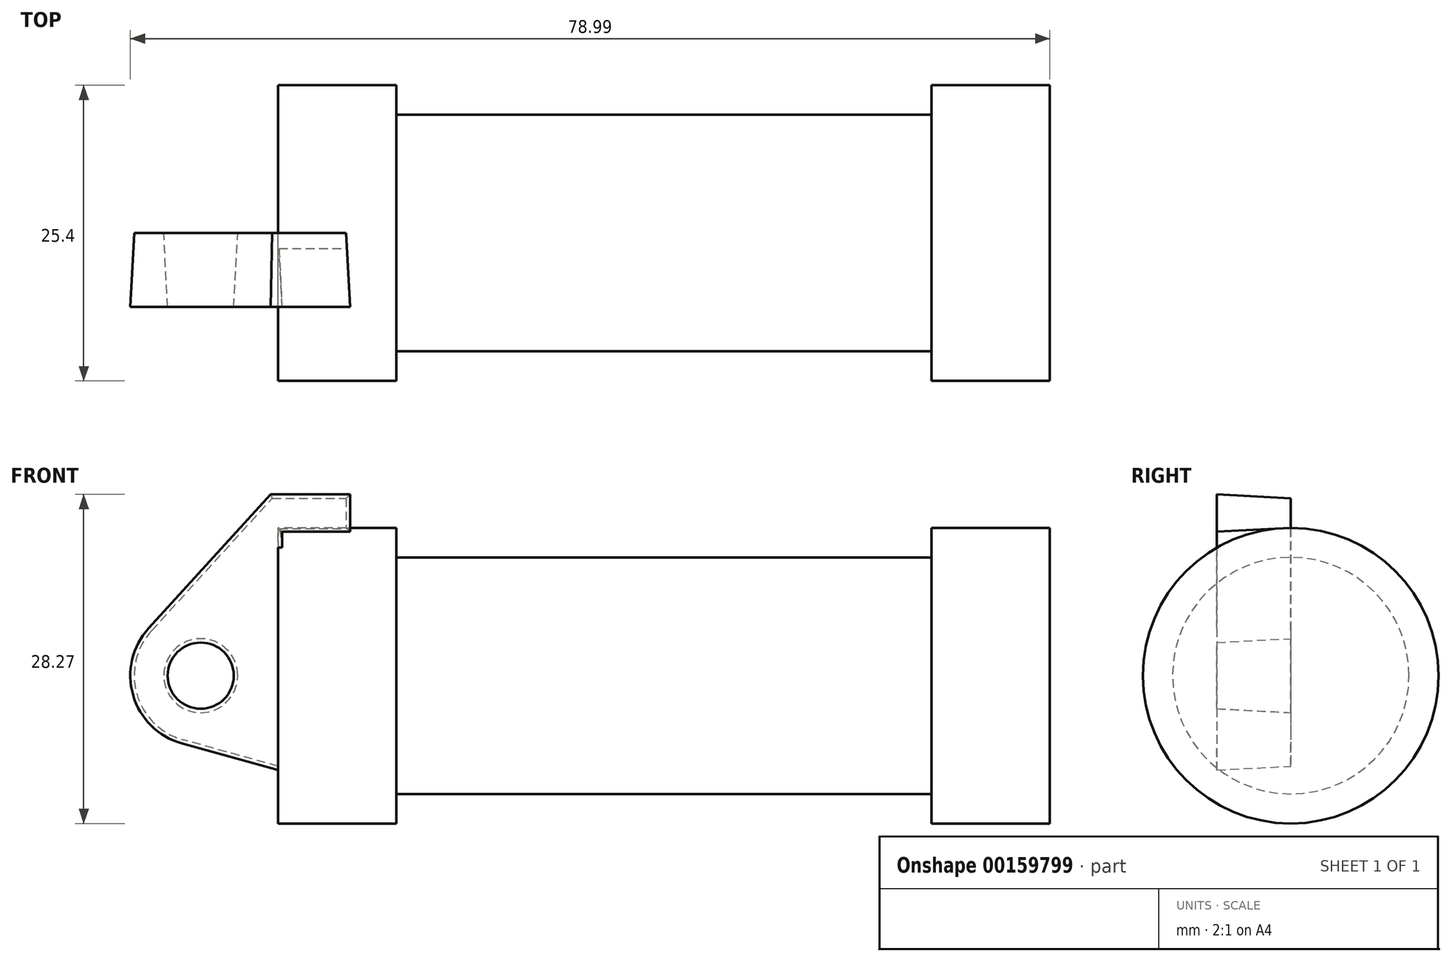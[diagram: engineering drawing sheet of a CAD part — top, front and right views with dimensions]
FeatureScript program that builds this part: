
annotation { "Feature Type Name" : "Feature", "Feature Type Description" : "" }
export const myFeature = defineFeature(function(context is Context, id is Id, definition is map)
    precondition{}
    {
        {
            var Q0;
            Q0=qCreatedBy(makeId("Front.planeOp"),FACE);
            var sketch = newSketch(context, id + "F0", { "sketchPlane" : qUnion([Q0])});
            skLineSegment(sketch, "E0", {"start": v(0, 0) * mm, "end": v(0, 12.7) * mm});
            skLineSegment(sketch, "E1", {"start": v(0, 12.7) * mm, "end": v(10.16, 12.7) * mm});
            skLineSegment(sketch, "E2", {"start": v(10.16, 12.7) * mm, "end": v(10.16, 10.16) * mm});
            skLineSegment(sketch, "E3", {"start": v(10.16, 10.16) * mm, "end": v(56.13, 10.16) * mm});
            skLineSegment(sketch, "E4", {"start": v(56.13, 10.16) * mm, "end": v(56.13, 12.7) * mm});
            skLineSegment(sketch, "E5", {"start": v(56.13, 12.7) * mm, "end": v(66.3, 12.7) * mm});
            skLineSegment(sketch, "E6", {"start": v(66.3, 12.7) * mm, "end": v(66.3, 0) * mm});
            skLineSegment(sketch, "E7", {"start": v(66.3, 0) * mm, "end": v(0, 0) * mm});
            skLineSegment(sketch, "E8", {"start": v(5.84, 15.24) * mm, "end": v(-0.5, 15.24) * mm});
            skLineSegment(sketch, "E9", {"start": v(-0.5, 15.24) * mm, "end": v(-10.88, 3.85) * mm});
            skLineSegment(sketch, "E10", {"start": v(0, 0) * mm, "end": v(-6.65, 0) * mm});
            skCircle(sketch, "E11", {"center": v(-6.65, 0) * mm, "radius": 5.72 * mm});
            skCircle(sketch, "E12", {"center": v(-6.65, 0) * mm, "radius": 3.18 * mm});
            skLineSegment(sketch, "E13", {"start": v(5.84, 15.24) * mm, "end": v(5.84, -9.4) * mm});
            skLineSegment(sketch, "E14", {"start": v(5.84, -9.4) * mm, "end": v(-8.18, -5.5) * mm});
            skSolve(sketch);
        }
        {
            var Q0;
            {var subQ0=sQuery(id+"F0.wireOp",EDGE,"E2");Q0=makeQuery(id+"F0.imprint","IMPRINT",FACE,{"disambiguationData":[TD([[makeQuery(id+"F0.imprint","IMPRINT",EDGE,{"derivedFrom":subQ0}),-1.0]])]});}
            var Q1;
            {var subQ0=sQuery(id+"F0.wireOp",EDGE,"E0");Q1=makeQuery(id+"F0.imprint","IMPRINT",FACE,{"disambiguationData":[TD([[makeQuery(id+"F0.imprint","IMPRINT",EDGE,{"derivedFrom":subQ0}),-1.0]])]});}
            var Q2;
            Q2=sQuery(id+"F0.wireOp",EDGE,"E7");
            revolve(context, id + "F1", {"entities" : qUnion([Q0, Q1]), "axis" : qUnion([Q2]), "revolveType" : RevolveType.FULL});
        }
        {
            var Q0;
            {var subQ3=sQuery(id+"F0.wireOp",EDGE,"E0");Q0=makeQuery(id+"F0.imprint","IMPRINT",FACE,{"disambiguationData":[TD([[makeQuery(id+"F0.imprint","IMPRINT",EDGE,{"derivedFrom":subQ3}),1.0]])]});}
            var Q1;
            {var subQ4=sQuery(id+"F0.wireOp",EDGE,"E12");Q1=makeQuery(id+"F0.imprint","IMPRINT",FACE,{"disambiguationData":[TD([[makeQuery(id+"F0.imprint","IMPRINT",EDGE,{"derivedFrom":subQ4}),-1.0]])]});}
            var Q2;
            {var subQ0=sQuery(id+"F0.wireOp",EDGE,"E14");Q2=makeQuery(id+"F0.imprint","IMPRINT",FACE,{"disambiguationData":[TD([[makeQuery(id+"F0.imprint","IMPRINT",EDGE,{"derivedFrom":subQ0}),-1.0]])]});}
            extrude(context, id + "F2", {"entities" : qUnion([Q0, Q1, Q2]), "operationType" : NewBodyOperationType.ADD, "depth" : 6.35 * mm, "hasDraft" : true, "draftAngle" : 3 * degree});
        }
    });
